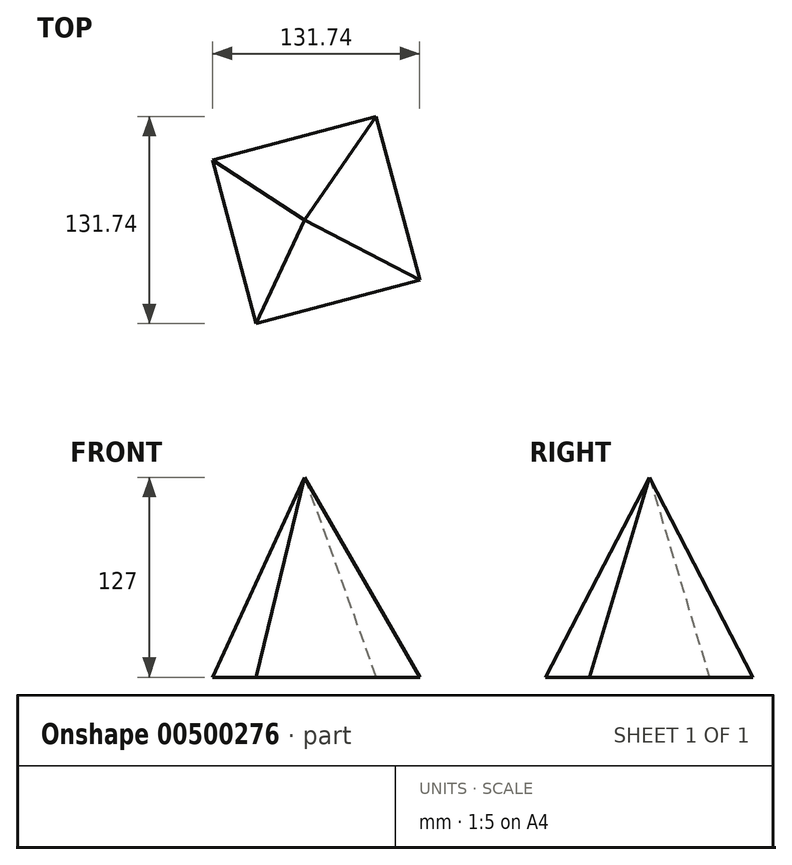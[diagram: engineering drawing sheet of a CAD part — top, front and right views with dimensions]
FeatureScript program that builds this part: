
annotation { "Feature Type Name" : "Feature", "Feature Type Description" : "" }
export const myFeature = defineFeature(function(context is Context, id is Id, definition is map)
    precondition{}
    {
        {
            var Q0;
            Q0=qCreatedBy(makeId("Top.planeOp"),FACE);
            var sketch = newSketch(context, id + "F0", { "sketchPlane" : qUnion([Q0])});
            skCircle(sketch, "E0.cCircle", {"center": v(0, 0) * mm, "radius": 76.07 * mm, "construction": true});
            skLineSegment(sketch, "E0.0", {"start": v(65.87, -38.04) * mm, "end": v(-38.04, -65.87) * mm});
            skLineSegment(sketch, "E0.1", {"start": v(-38.04, -65.87) * mm, "end": v(-65.87, 38.04) * mm});
            skLineSegment(sketch, "E0.2", {"start": v(-65.87, 38.04) * mm, "end": v(38.04, 65.87) * mm});
            skLineSegment(sketch, "E0.3", {"start": v(38.04, 65.87) * mm, "end": v(65.87, -38.04) * mm});
            skSolve(sketch);
        }
        {
            var Q0;
            Q0=qCreatedBy(makeId("Top.planeOp"),FACE);
            cPlane(context, id + "F1", {"entities" : qUnion([Q0]), "cplaneType" : CPlaneType.OFFSET, "offset" : 127 * mm, "width" : 152.4 * mm, "height" : 152.4 * mm});
        }
        {
            var Q0;
            Q0=qCreatedBy(id+"F1.planeOp",FACE);
            var sketch = newSketch(context, id + "F2", { "sketchPlane" : qUnion([Q0])});
            skPoint(sketch, "E1", {"position": v(-7.21, 0) * mm});
            skSolve(sketch);
        }
        {
            var Q0;
            Q0=sQuery(id+"F2.wireOp",VERTEX,"E1");
            var Q1;
            Q1=makeQuery(id+"F0.imprint","IMPRINT",FACE,{"disambiguationData":[TD([[makeQuery(id+"F0.imprint","IMPRINT",EDGE,{"derivedFrom":sQuery(id+"F0.wireOp",EDGE,"E0.0")}),-1.0]])]});
            loft(context, id + "F3", {"sheetProfilesArray" : [{ "sheetProfileEntities" : qUnion([Q0]) }, { "sheetProfileEntities" : qUnion([Q1]) }]});
        }
    });
